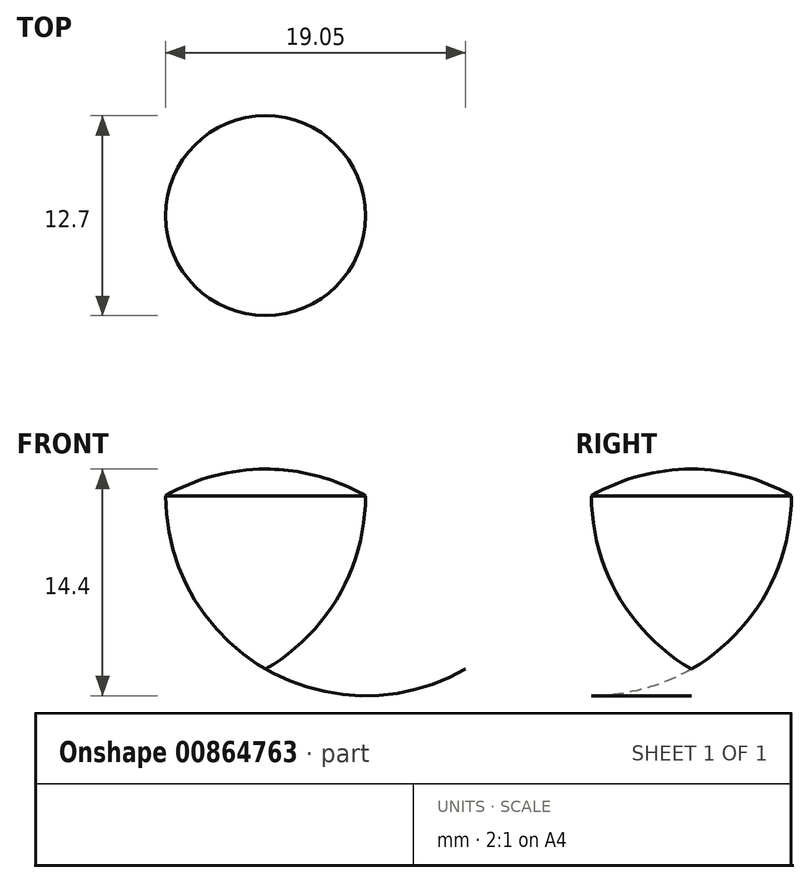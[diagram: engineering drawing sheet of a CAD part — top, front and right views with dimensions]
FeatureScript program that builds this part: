
annotation { "Feature Type Name" : "Feature", "Feature Type Description" : "" }
export const myFeature = defineFeature(function(context is Context, id is Id, definition is map)
    precondition{}
    {
        {
            var Q0;
            Q0=qCreatedBy(makeId("Front.planeOp"),FACE);
            var sketch = newSketch(context, id + "F0", { "sketchPlane" : qUnion([Q0])});
            skCircle(sketch, "E0", {"center": v(0, 0) * mm, "radius": 12.7 * mm});
            skCircle(sketch, "E1", {"center": v(12.7, 0) * mm, "radius": 12.7 * mm});
            skCircle(sketch, "E2", {"center": v(6.35, -11) * mm, "radius": 12.7 * mm});
            skLineSegment(sketch, "E3", {"start": v(6.35, 1.7) * mm, "end": v(6.35, -11) * mm});
            skSolve(sketch);
        }
        {
            var Q0;
            {var subQ0=sQuery(id+"F0.wireOp",EDGE,"E3");Q0=makeQuery(id+"F0.imprint","IMPRINT",FACE,{"disambiguationData":[TD([[makeQuery(id+"F0.imprint","IMPRINT",EDGE,{"derivedFrom":subQ0}),1.0]])]});}
            var Q1;
            Q1=sQuery(id+"F0.wireOp",EDGE,"E3");
            revolve(context, id + "F1", {"surfaceOperationType" : NewSurfaceOperationType.NEW, "entities" : qUnion([Q0]), "axis" : qUnion([Q1]), "revolveType" : RevolveType.FULL});
        }
    });
